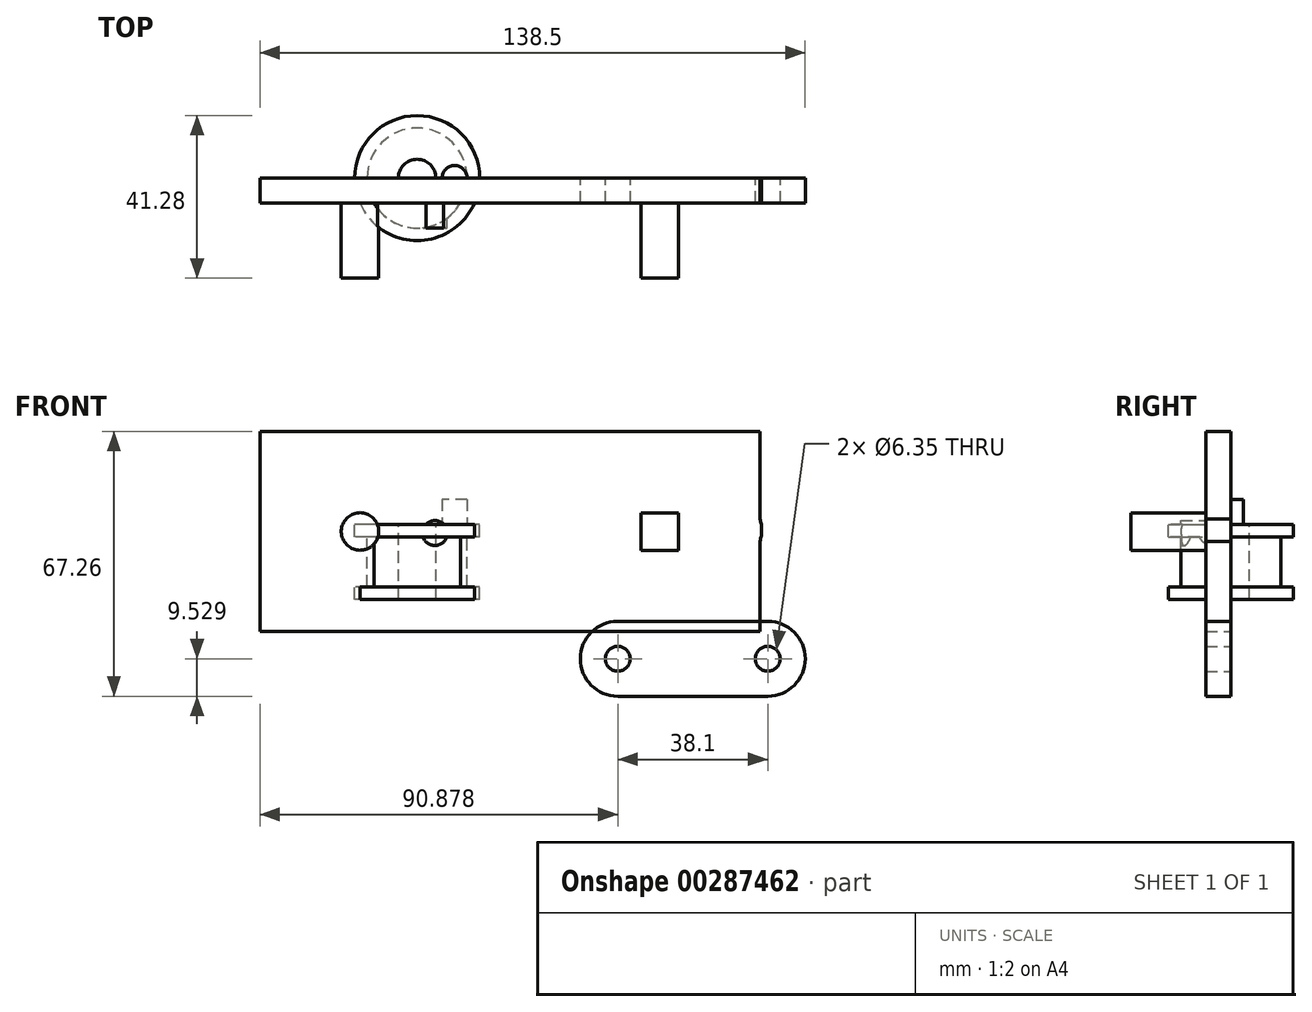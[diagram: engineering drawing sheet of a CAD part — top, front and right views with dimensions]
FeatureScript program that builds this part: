
annotation { "Feature Type Name" : "Feature", "Feature Type Description" : "" }
export const myFeature = defineFeature(function(context is Context, id is Id, definition is map)
    precondition{}
    {
        {
            var Q0;
            Q0=qCreatedBy(makeId("Front.planeOp"),FACE);
            var sketch = newSketch(context, id + "F0", { "sketchPlane" : qUnion([Q0])});
            skLineSegment(sketch, "E0.bottom", {"start": v(-86.15, 51.6) * mm, "end": v(40.85, 51.6) * mm});
            skLineSegment(sketch, "E0.top", {"start": v(-86.15, 0.8) * mm, "end": v(40.85, 0.8) * mm});
            skLineSegment(sketch, "E0.left", {"start": v(-86.15, 51.6) * mm, "end": v(-86.15, 0.8) * mm});
            skLineSegment(sketch, "E0.right", {"start": v(40.85, 51.6) * mm, "end": v(40.85, 0.8) * mm});
            skCircle(sketch, "E1", {"center": v(-60.75, 26.2) * mm, "radius": 4.76 * mm});
            skLineSegment(sketch, "E2.bottom", {"start": v(10.7, 30.97) * mm, "end": v(20.22, 30.97) * mm});
            skLineSegment(sketch, "E2.top", {"start": v(10.7, 21.44) * mm, "end": v(20.22, 21.44) * mm});
            skLineSegment(sketch, "E2.left", {"start": v(10.7, 30.97) * mm, "end": v(10.7, 21.44) * mm});
            skLineSegment(sketch, "E2.right", {"start": v(20.22, 30.97) * mm, "end": v(20.22, 21.44) * mm});
            skLineSegment(sketch, "E3", {"start": v(10.7, 21.44) * mm, "end": v(15.45, 21.44) * mm});
            skLineSegment(sketch, "E4", {"start": v(20.22, 21.44) * mm, "end": v(20.22, 26.2) * mm});
            skSolve(sketch);
        }
        {
            var Q0;
            Q0=makeQuery(id+"F0.imprint","IMPRINT",FACE,{"disambiguationData":[TD([[makeQuery(id+"F0.imprint","IMPRINT",EDGE,{"derivedFrom":sQuery(id+"F0.wireOp",EDGE,"E0.bottom")}),-1.0]])]});
            extrude(context, id + "F1", {"entities" : qUnion([Q0]), "depth" : 6.35 * mm});
        }
        {
            var Q0;
            Q0=makeQuery(id+"F0.imprint","IMPRINT",FACE,{"disambiguationData":[TD([[makeQuery(id+"F0.imprint","IMPRINT",EDGE,{"derivedFrom":sQuery(id+"F0.wireOp",EDGE,"E1")}),1.0]])]});
            var Q1;
            Q1=makeQuery(id+"F0.imprint","IMPRINT",FACE,{"disambiguationData":[TD([[makeQuery(id+"F0.imprint","IMPRINT",EDGE,{"derivedFrom":sQuery(id+"F0.wireOp",EDGE,"E2.bottom")}),-1.0]])]});
            extrude(context, id + "F2", {"entities" : qUnion([Q0, Q1]), "operationType" : NewBodyOperationType.ADD, "depth" : 25.4 * mm});
        }
        {
            var Q0;
            Q0=qCreatedBy(makeId("Front.planeOp"),FACE);
            var sketch = newSketch(context, id + "F3", { "sketchPlane" : qUnion([Q0])});
            skLineSegment(sketch, "E5.bottom", {"start": v(4.73, 3.4) * mm, "end": v(42.83, 3.4) * mm});
            skLineSegment(sketch, "E5.top", {"start": v(4.73, -15.66) * mm, "end": v(42.83, -15.66) * mm});
            skLineSegment(sketch, "E5.left", {"start": v(4.73, 3.4) * mm, "end": v(4.73, -15.66) * mm});
            skLineSegment(sketch, "E5.right", {"start": v(42.83, 3.4) * mm, "end": v(42.83, -15.66) * mm});
            skArc(sketch, "E6", {"start": v(42.83, -15.66) * mm, "mid": v(52.35, -6.13) * mm, "end": v(42.83, 3.4) * mm});
            skArc(sketch, "E7", {"start": v(4.73, 3.4) * mm, "mid": v(-4.8, -6.13) * mm, "end": v(4.73, -15.66) * mm});
            skCircle(sketch, "E8", {"center": v(4.73, -6.13) * mm, "radius": 3.18 * mm});
            skCircle(sketch, "E9", {"center": v(42.83, -6.13) * mm, "radius": 3.18 * mm});
            skSolve(sketch);
        }
        {
            var Q0;
            {var subQ0=sQuery(id+"F3.wireOp",EDGE,"E7");Q0=makeQuery(id+"F3.imprint","IMPRINT",FACE,{"disambiguationData":[TD([[makeQuery(id+"F3.imprint","IMPRINT",EDGE,{"derivedFrom":subQ0}),1.0]])]});}
            var Q1;
            {var subQ5=sQuery(id+"F3.wireOp",EDGE,"E5.bottom");Q1=makeQuery(id+"F3.imprint","IMPRINT",FACE,{"disambiguationData":[TD([[makeQuery(id+"F3.imprint","IMPRINT",EDGE,{"derivedFrom":subQ5}),-1.0]])]});}
            var Q2;
            {var subQ0=sQuery(id+"F3.wireOp",EDGE,"E6");Q2=makeQuery(id+"F3.imprint","IMPRINT",FACE,{"disambiguationData":[TD([[makeQuery(id+"F3.imprint","IMPRINT",EDGE,{"derivedFrom":subQ0}),1.0]])]});}
            extrude(context, id + "F4", {"entities" : qUnion([Q0, Q1, Q2]), "depth" : 6.35 * mm});
        }
        {
            var Q0;
            Q0=qCreatedBy(makeId("Front.planeOp"),FACE);
            var sketch = newSketch(context, id + "F5", { "sketchPlane" : qUnion([Q0])});
            skLineSegment(sketch, "E10.bottom", {"start": v(-44.43, 36.07) * mm, "end": v(31.77, 36.07) * mm});
            skLineSegment(sketch, "E10.top", {"start": v(-44.43, 17.02) * mm, "end": v(31.77, 17.02) * mm});
            skLineSegment(sketch, "E10.left", {"start": v(-44.43, 36.07) * mm, "end": v(-44.43, 17.02) * mm});
            skLineSegment(sketch, "E10.right", {"start": v(31.77, 36.07) * mm, "end": v(31.77, 17.02) * mm});
            skArc(sketch, "E11", {"start": v(31.77, 17.02) * mm, "mid": v(41.3, 26.55) * mm, "end": v(31.77, 36.07) * mm});
            skArc(sketch, "E12", {"start": v(-44.43, 36.07) * mm, "mid": v(-53.96, 26.55) * mm, "end": v(-44.43, 17.02) * mm});
            skCircle(sketch, "E13", {"center": v(31.77, 26.55) * mm, "radius": 3.18 * mm});
            skCircle(sketch, "E14", {"center": v(-44.43, 26.55) * mm, "radius": 3.18 * mm});
            skLineSegment(sketch, "E15.bottom", {"start": v(-31.73, 31.3) * mm, "end": v(19.07, 31.3) * mm});
            skLineSegment(sketch, "E15.top", {"start": v(-31.73, 21.78) * mm, "end": v(19.07, 21.78) * mm});
            skLineSegment(sketch, "E15.left", {"start": v(-31.73, 31.3) * mm, "end": v(-31.73, 21.78) * mm});
            skLineSegment(sketch, "E15.right", {"start": v(19.07, 31.3) * mm, "end": v(19.07, 21.78) * mm});
            skLineSegment(sketch, "E16", {"start": v(-44.43, 17.02) * mm, "end": v(-6.33, 17.02) * mm});
            skLineSegment(sketch, "E17", {"start": v(19.07, 21.78) * mm, "end": v(-6.33, 21.78) * mm});
            skArc(sketch, "E18", {"start": v(19.07, 21.78) * mm, "mid": v(23.83, 26.55) * mm, "end": v(19.07, 31.3) * mm});
            skArc(sketch, "E19", {"start": v(-31.73, 31.3) * mm, "mid": v(-36.5, 26.55) * mm, "end": v(-31.73, 21.78) * mm});
            skSolve(sketch);
        }
        {
            var Q0;
            {var subQ0=sQuery(id+"F5.wireOp",EDGE,"E12");Q0=makeQuery(id+"F5.imprint","IMPRINT",FACE,{"disambiguationData":[TD([[makeQuery(id+"F5.imprint","IMPRINT",EDGE,{"derivedFrom":subQ0}),1.0]])]});}
            var Q1;
            {var subQ6=sQuery(id+"F5.wireOp",EDGE,"E10.bottom");Q1=makeQuery(id+"F5.imprint","IMPRINT",FACE,{"disambiguationData":[TD([[makeQuery(id+"F5.imprint","IMPRINT",EDGE,{"derivedFrom":subQ6}),-1.0]])]});}
            var Q2;
            {var subQ0=sQuery(id+"F5.wireOp",EDGE,"E11");Q2=makeQuery(id+"F5.imprint","IMPRINT",FACE,{"disambiguationData":[TD([[makeQuery(id+"F5.imprint","IMPRINT",EDGE,{"derivedFrom":subQ0}),1.0]])]});}
            extrude(context, id + "F6", {"entities" : qUnion([Q0, Q1, Q2]), "depth" : 6.35 * mm});
        }
        {
            var Q0;
            Q0=qCreatedBy(makeId("Front.planeOp"),FACE);
            var sketch = newSketch(context, id + "F7", { "sketchPlane" : qUnion([Q0])});
            skCircle(sketch, "E20", {"center": v(-41.73, 25.8) * mm, "radius": 3.18 * mm});
            skSolve(sketch);
        }
        {
            var Q0;
            Q0=makeQuery(id+"F7.imprint","IMPRINT",FACE,{"disambiguationData":[TD([[makeQuery(id+"F7.imprint","IMPRINT",EDGE,{"derivedFrom":sQuery(id+"F7.wireOp",EDGE,"E20")}),1.0]])]});
            extrude(context, id + "F8", {"entities" : qUnion([Q0]), "depth" : 12.7 * mm});
        }
        {
            var Q0;
            Q0=qCreatedBy(makeId("Front.planeOp"),FACE);
            var sketch = newSketch(context, id + "F9", { "sketchPlane" : qUnion([Q0])});
            skLineSegment(sketch, "E21.bottom", {"start": v(-62.11, 28.04) * mm, "end": v(-30.36, 28.04) * mm});
            skLineSegment(sketch, "E21.top", {"start": v(-62.11, 24.87) * mm, "end": v(-30.36, 24.87) * mm});
            skLineSegment(sketch, "E21.left", {"start": v(-62.11, 28.04) * mm, "end": v(-62.11, 24.87) * mm});
            skLineSegment(sketch, "E21.right", {"start": v(-30.36, 28.04) * mm, "end": v(-30.36, 24.87) * mm});
            skLineSegment(sketch, "E22.bottom", {"start": v(-62.11, 12.17) * mm, "end": v(-30.36, 12.17) * mm});
            skLineSegment(sketch, "E22.top", {"start": v(-62.11, 9) * mm, "end": v(-30.36, 9) * mm});
            skLineSegment(sketch, "E22.left", {"start": v(-62.11, 12.17) * mm, "end": v(-62.11, 9) * mm});
            skLineSegment(sketch, "E22.right", {"start": v(-30.36, 12.17) * mm, "end": v(-30.36, 9) * mm});
            skLineSegment(sketch, "E23.bottom", {"start": v(-58.94, 24.87) * mm, "end": v(-33.54, 24.87) * mm});
            skLineSegment(sketch, "E23.top", {"start": v(-58.94, 12.17) * mm, "end": v(-33.54, 12.17) * mm});
            skLineSegment(sketch, "E23.left", {"start": v(-58.94, 24.87) * mm, "end": v(-58.94, 12.17) * mm});
            skLineSegment(sketch, "E23.right", {"start": v(-33.54, 24.87) * mm, "end": v(-33.54, 12.17) * mm});
            skLineSegment(sketch, "E24.bottom", {"start": v(-51, 28.04) * mm, "end": v(-41.48, 28.04) * mm});
            skLineSegment(sketch, "E24.top", {"start": v(-51, 9) * mm, "end": v(-41.48, 9) * mm});
            skLineSegment(sketch, "E24.left", {"start": v(-51, 28.04) * mm, "end": v(-51, 9) * mm});
            skLineSegment(sketch, "E24.right", {"start": v(-41.48, 28.04) * mm, "end": v(-41.48, 9) * mm});
            skLineSegment(sketch, "E25", {"start": v(-46.24, 28.04) * mm, "end": v(-46.24, 9) * mm});
            skSolve(sketch);
        }
        {
            var Q0;
            {var subQ5=sQuery(id+"F9.wireOp",EDGE,"E21.right");Q0=makeQuery(id+"F9.imprint","IMPRINT",FACE,{"disambiguationData":[TD([[makeQuery(id+"F9.imprint","IMPRINT",EDGE,{"derivedFrom":subQ5}),-1.0]])]});}
            var Q1;
            {var subQ0=sQuery(id+"F9.wireOp",EDGE,"E23.right");Q1=makeQuery(id+"F9.imprint","IMPRINT",FACE,{"disambiguationData":[TD([[makeQuery(id+"F9.imprint","IMPRINT",EDGE,{"derivedFrom":subQ0}),-1.0]])]});}
            var Q2;
            {var subQ0=sQuery(id+"F9.wireOp",EDGE,"E22.right");Q2=makeQuery(id+"F9.imprint","IMPRINT",FACE,{"disambiguationData":[TD([[makeQuery(id+"F9.imprint","IMPRINT",EDGE,{"derivedFrom":subQ0}),-1.0]])]});}
            var Q3;
            Q3=sQuery(id+"F9.wireOp",EDGE,"E25");
            revolve(context, id + "F10", {"entities" : qUnion([Q0, Q1, Q2]), "axis" : qUnion([Q3]), "revolveType" : RevolveType.FULL});
        }
        {
            var Q0;
            Q0=makeQuery(id+"F10.opRevolve","SWEPT_FACE",FACE,{"disambiguationData":[OSD([sQuery(id+"F9.wireOp",EDGE,"E21.bottom")])]});
            var sketch = newSketch(context, id + "F11", { "sketchPlane" : qUnion([Q0])});
            skCircle(sketch, "E26", {"center": v(-36.71, 0) * mm, "radius": 3.18 * mm});
            skSolve(sketch);
        }
        {
            var Q0;
            Q0=makeQuery(id+"F11.imprint","IMPRINT",FACE,{"disambiguationData":[TD([[makeQuery(id+"F11.imprint","IMPRINT",EDGE,{"derivedFrom":sQuery(id+"F11.wireOp",EDGE,"E26")}),1.0]])]});
            extrude(context, id + "F12", {"entities" : qUnion([Q0]), "operationType" : NewBodyOperationType.ADD, "depth" : 6.35 * mm});
        }
    });
